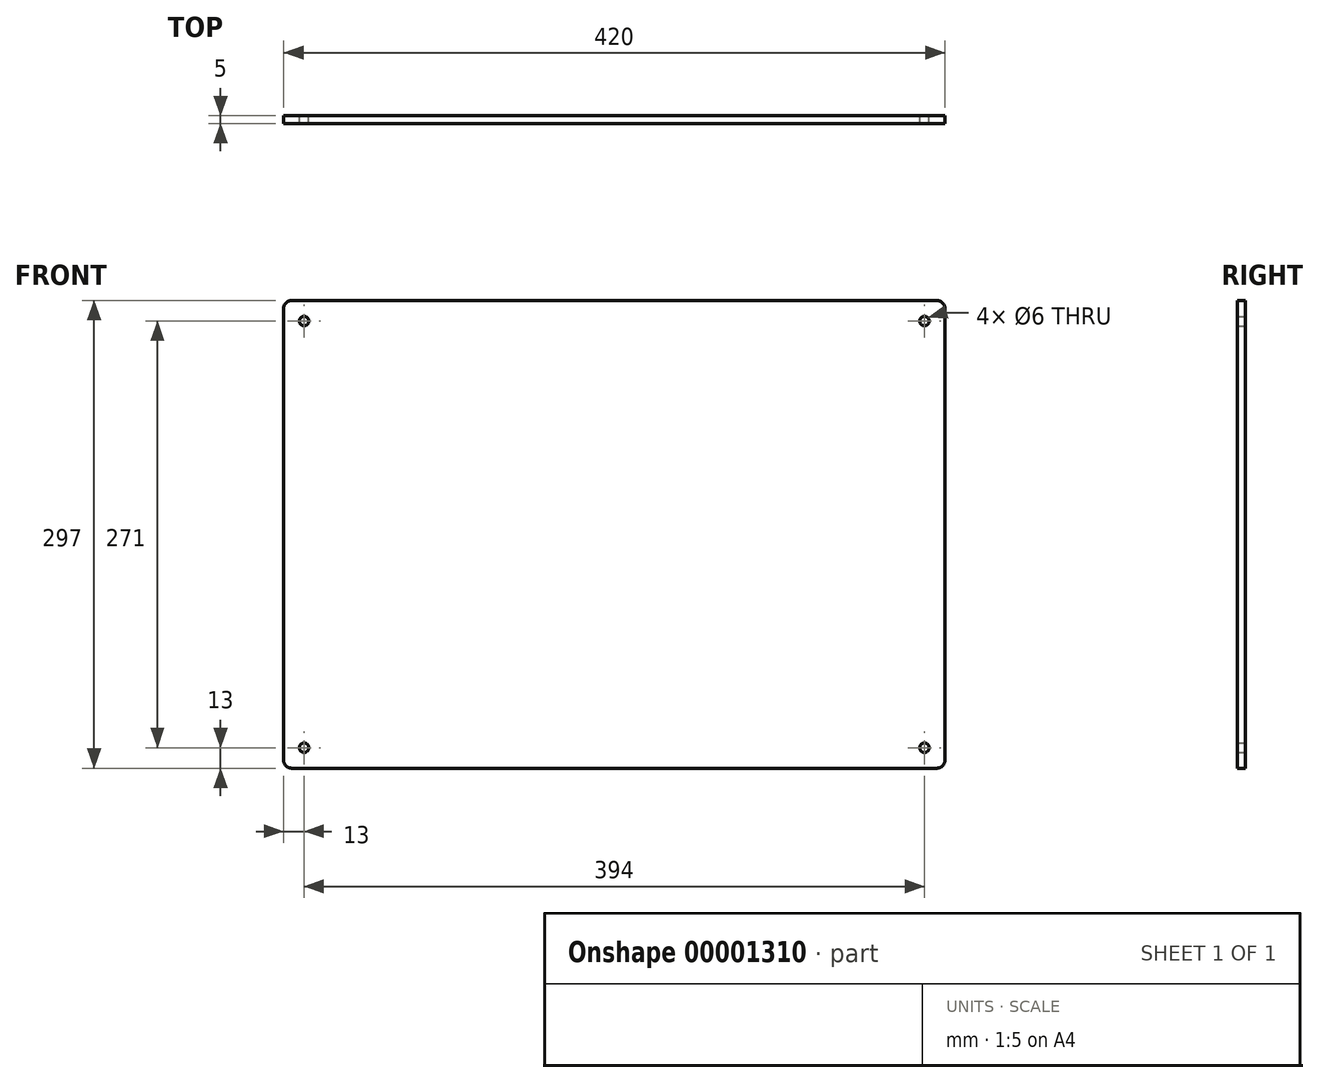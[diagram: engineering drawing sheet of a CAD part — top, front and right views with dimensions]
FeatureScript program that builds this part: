
annotation { "Feature Type Name" : "Feature", "Feature Type Description" : "" }
export const myFeature = defineFeature(function(context is Context, id is Id, definition is map)
    precondition{}
    {
        {
            var Q0;
            Q0=qCreatedBy(makeId("Front.planeOp"),FACE);
            var sketch = newSketch(context, id + "F0", { "sketchPlane" : qUnion([Q0])});
            skLineSegment(sketch, "E0.bottom", {"start": v(420.5, -594.5) * mm, "end": v(-420.5, -594.5) * mm});
            skLineSegment(sketch, "E0.top", {"start": v(420.5, 594.5) * mm, "end": v(-420.5, 594.5) * mm});
            skLineSegment(sketch, "E0.left", {"start": v(420.5, -594.5) * mm, "end": v(420.5, 594.5) * mm});
            skLineSegment(sketch, "E0.right", {"start": v(-420.5, -594.5) * mm, "end": v(-420.5, 594.5) * mm});
            skPoint(sketch, "E0.middle", {"position": v(0, 0) * mm});
            skSolve(sketch);
        }
        {
            var Q0;
            Q0=qCreatedBy(makeId("Front.planeOp"),FACE);
            var sketch = newSketch(context, id + "F1", { "sketchPlane" : qUnion([Q0])});
            skLineSegment(sketch, "E1.bottom", {"start": v(-420, 0) * mm, "end": v(0, 0) * mm});
            skLineSegment(sketch, "E1.top", {"start": v(-420, 297) * mm, "end": v(0, 297) * mm});
            skLineSegment(sketch, "E1.left", {"start": v(-420, 0) * mm, "end": v(-420, 297) * mm});
            skLineSegment(sketch, "E1.right", {"start": v(0, 0) * mm, "end": v(0, 297) * mm});
            skCircle(sketch, "E2", {"center": v(-407, 284) * mm, "radius": 3 * mm});
            skCircle(sketch, "E3", {"center": v(-407, 13) * mm, "radius": 3 * mm});
            skCircle(sketch, "E4", {"center": v(-13, 284) * mm, "radius": 3 * mm});
            skCircle(sketch, "E5", {"center": v(-13, 13) * mm, "radius": 3 * mm});
            skSolve(sketch);
        }
        {
            var Q0;
            Q0=makeQuery(id+"F1.imprint","IMPRINT",FACE,{"disambiguationData":[TD([[makeQuery(id+"F1.imprint","IMPRINT",EDGE,{"derivedFrom":sQuery(id+"F1.wireOp",EDGE,"E1.bottom")}),1.0]])]});
            extrude(context, id + "F2", {"entities" : qUnion([Q0]), "depth" : 5 * mm});
        }
        {
            var Q0;
            Q0=makeQuery(id+"F2.opExtrude","SWEPT_EDGE",EDGE,{"disambiguationData":[OSD([sQuery(id+"F1.wireOp",EDGE,"E1.bottom"),sQuery(id+"F1.wireOp",EDGE,"E1.left")])]});
            var Q1;
            Q1=makeQuery(id+"F2.opExtrude","SWEPT_EDGE",EDGE,{"disambiguationData":[OSD([sQuery(id+"F1.wireOp",EDGE,"E1.top"),sQuery(id+"F1.wireOp",EDGE,"E1.right")])]});
            var Q2;
            Q2=makeQuery(id+"F2.opExtrude","SWEPT_EDGE",EDGE,{"disambiguationData":[OSD([sQuery(id+"F1.wireOp",EDGE,"E1.bottom"),sQuery(id+"F1.wireOp",EDGE,"E1.right")])]});
            var Q3;
            Q3=makeQuery(id+"F2.opExtrude","SWEPT_EDGE",EDGE,{"disambiguationData":[OSD([sQuery(id+"F1.wireOp",EDGE,"E1.top"),sQuery(id+"F1.wireOp",EDGE,"E1.left")])]});
            fillet(context, id + "F3", {"entities" : qUnion([Q0, Q1, Q2, Q3]), "radius" : 5 * mm, "tangentPropagation" : true, "allowEdgeOverflow" : false});
        }
    });
